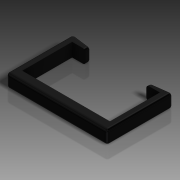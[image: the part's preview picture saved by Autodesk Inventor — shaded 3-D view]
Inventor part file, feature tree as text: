
AUTODESK INVENTOR PART (.ipt)
format: ipt  version: 2015 (Build 190159000, 159)  size: 155,136 bytes
history: native  units: mm
features: fillet x3, extrude x1, direct_edit x1, sketch x1, move_body x1
ambient origin geometry x8: Origin, YZ Plane, XZ Plane, XY Plane, X Axis, Y Axis, Z Axis, Center Point
bodies: Volumenkörper1 (feature_tree)
feature tree (7):
  extrude  "Extrusion1"  Depth=37.0mm
  fillet  "Rundung1"  Radius=10.0mm
  fillet  "Rundung2"  Radius=7.0mm
  fillet  "Rundung3"  Radius=5.0mm
  direct_edit  "Direktbearbeitung1"
  sketch  "Skizze1"  dims[d0=65.0mm d1=37.0mm d3=10.0mm d4=7.0mm d5=5.0mm d6=3.0mm d7=20.0mm d8=0.0mm d9=2.0mm d10=2.0mm d11=2.0mm d12=0.0mm d13=0.0mm d14=-10.0mm]
  move_body  "Verschieben1"
